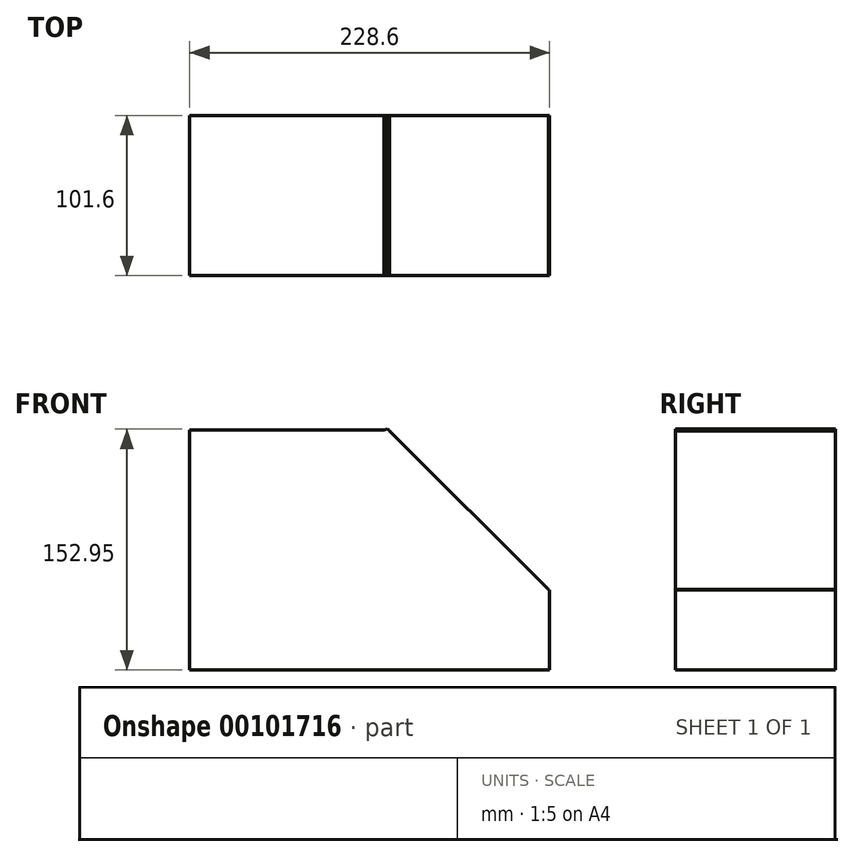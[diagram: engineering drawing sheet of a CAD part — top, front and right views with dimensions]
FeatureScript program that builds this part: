
annotation { "Feature Type Name" : "Feature", "Feature Type Description" : "" }
export const myFeature = defineFeature(function(context is Context, id is Id, definition is map)
    precondition{}
    {
        {
            var Q0;
            Q0=qCreatedBy(makeId("Front.planeOp"),FACE);
            var sketch = newSketch(context, id + "F0", { "sketchPlane" : qUnion([Q0])});
            skLineSegment(sketch, "E0", {"start": v(-57.33, 40.34) * mm, "end": v(-57.33, -112.06) * mm});
            skLineSegment(sketch, "E1", {"start": v(-57.33, -112.06) * mm, "end": v(69.67, -112.06) * mm});
            skLineSegment(sketch, "E2", {"start": v(69.67, -112.06) * mm, "end": v(69.67, 40.34) * mm});
            skLineSegment(sketch, "E3", {"start": v(69.67, 40.34) * mm, "end": v(-57.33, 40.34) * mm});
            skSolve(sketch);
        }
        {
            var Q0;
            Q0=makeQuery(id+"F0.imprint","IMPRINT",FACE,{"disambiguationData":[TD([[makeQuery(id+"F0.imprint","IMPRINT",EDGE,{"derivedFrom":sQuery(id+"F0.wireOp",EDGE,"E0")}),1.0]])]});
            extrude(context, id + "F1", {"entities" : qUnion([Q0]), "depth" : 101.6 * mm});
        }
        {
            var Q0;
            Q0=makeQuery(id+"F1.opExtrude","SWEPT_FACE",FACE,{"disambiguationData":[OSD([sQuery(id+"F0.wireOp",EDGE,"E2")])]});
            var sketch = newSketch(context, id + "F2", { "sketchPlane" : qUnion([Q0])});
            skLineSegment(sketch, "E4.bottom", {"start": v(-101.6, -112.06) * mm, "end": v(0, -112.06) * mm});
            skLineSegment(sketch, "E4.top", {"start": v(-101.6, -61.26) * mm, "end": v(0, -61.26) * mm});
            skLineSegment(sketch, "E4.left", {"start": v(-101.6, -112.06) * mm, "end": v(-101.6, -61.26) * mm});
            skLineSegment(sketch, "E4.right", {"start": v(0, -112.06) * mm, "end": v(0, -61.26) * mm});
            skSolve(sketch);
        }
        {
            var Q0;
            Q0=makeQuery(id+"F2.imprint","IMPRINT",FACE,{"disambiguationData":[TD([[makeQuery(id+"F2.imprint","IMPRINT",EDGE,{"derivedFrom":sQuery(id+"F2.wireOp",EDGE,"E4.bottom")}),1.0]])]});
            extrude(context, id + "F3", {"entities" : qUnion([Q0]), "operationType" : NewBodyOperationType.ADD, "depth" : 101.6 * mm});
        }
        {
            var Q0;
            Q0=qCreatedBy(makeId("Front.planeOp"),FACE);
            var sketch = newSketch(context, id + "F4", { "sketchPlane" : qUnion([Q0])});
            skLineSegment(sketch, "E5", {"start": v(-30.26, 17.66) * mm, "end": v(67.37, -89.13) * mm});
            skLineSegment(sketch, "E6", {"start": v(67.37, -89.13) * mm, "end": v(170.63, -61.11) * mm});
            skLineSegment(sketch, "E7", {"start": v(170.63, -61.11) * mm, "end": v(68.38, 40.89) * mm});
            skLineSegment(sketch, "E8", {"start": v(68.38, 40.89) * mm, "end": v(-30.26, 17.66) * mm});
            skSolve(sketch);
        }
        {
            var Q0;
            Q0=makeQuery(id+"F4.imprint","IMPRINT",FACE,{"disambiguationData":[TD([[makeQuery(id+"F4.imprint","IMPRINT",EDGE,{"derivedFrom":sQuery(id+"F4.wireOp",EDGE,"E5")}),1.0]])]});
            extrude(context, id + "F5", {"entities" : qUnion([Q0]), "operationType" : NewBodyOperationType.ADD, "depth" : 101.6 * mm});
        }
    });
